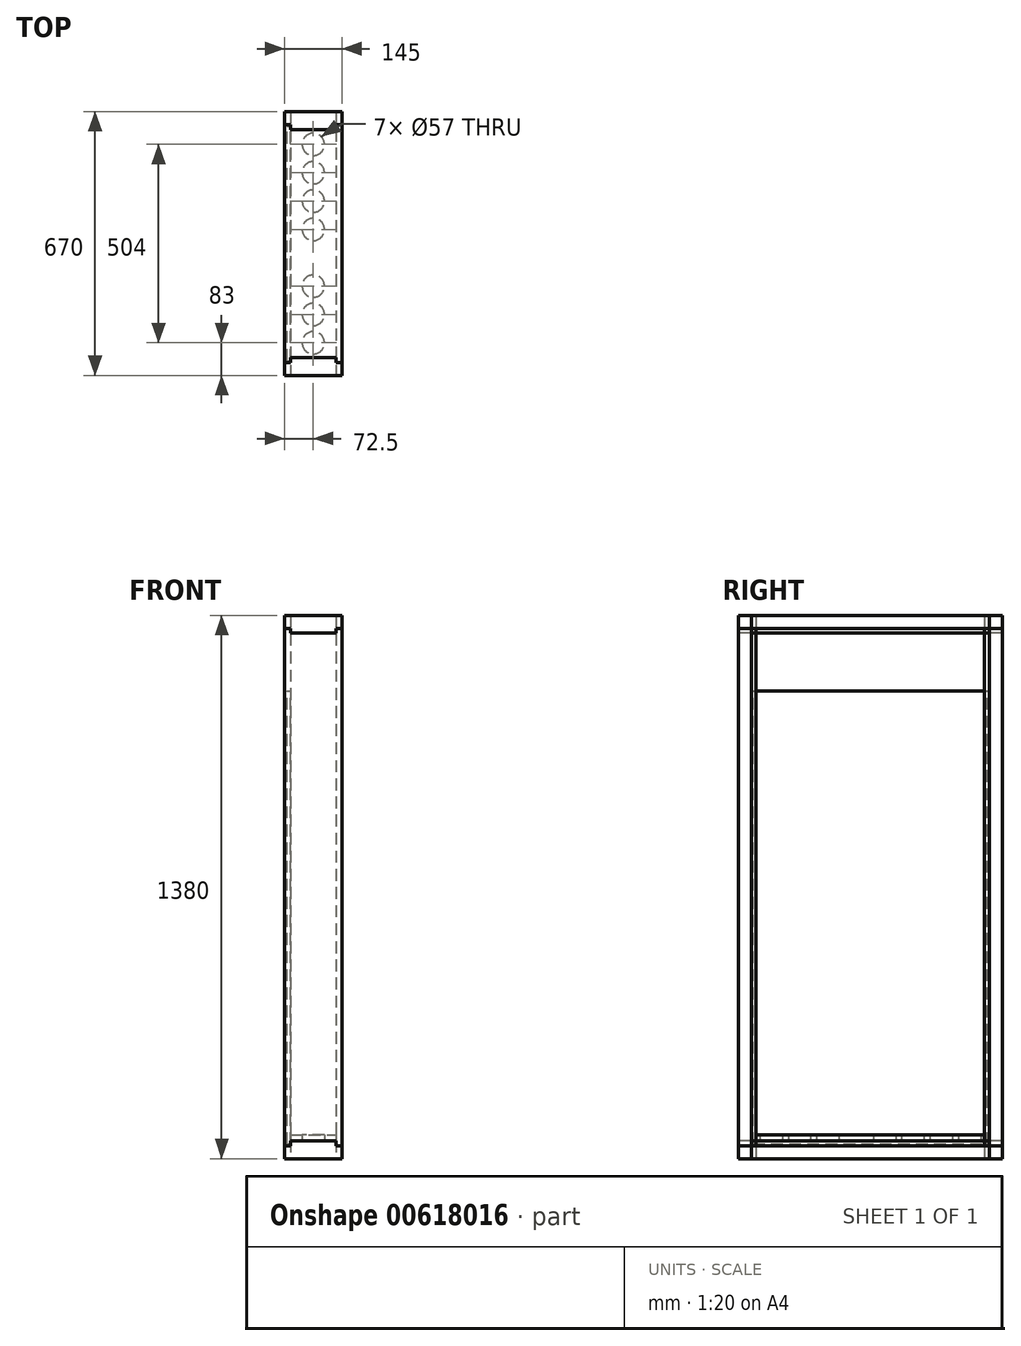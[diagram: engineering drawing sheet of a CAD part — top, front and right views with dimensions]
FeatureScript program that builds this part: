
annotation { "Feature Type Name" : "Feature", "Feature Type Description" : "" }
export const myFeature = defineFeature(function(context is Context, id is Id, definition is map)
    precondition{}
    {
        {
            var Q0;
            Q0=qCreatedBy(makeId("Top.planeOp"),FACE);
            var sketch = newSketch(context, id + "F0", { "sketchPlane" : qUnion([Q0])});
            skLineSegment(sketch, "E0.bottom", {"start": v(0, 0) * mm, "end": v(145, 0) * mm});
            skLineSegment(sketch, "E0.top", {"start": v(15, 45) * mm, "end": v(130, 45) * mm});
            skLineSegment(sketch, "E0.left", {"start": v(0, 0) * mm, "end": v(0, 33) * mm});
            skLineSegment(sketch, "E0.right", {"start": v(145, 0) * mm, "end": v(145, 33) * mm});
            skLineSegment(sketch, "E1.0", {"start": v(15, 33) * mm, "end": v(15, 45) * mm});
            skLineSegment(sketch, "E2.0", {"start": v(0, 33) * mm, "end": v(15, 33) * mm});
            skLineSegment(sketch, "E3.MirrorCS", {"start": v(145, 33) * mm, "end": v(130, 33) * mm});
            skLineSegment(sketch, "E4.MirrorCS", {"start": v(130, 33) * mm, "end": v(130, 45) * mm});
            skPoint(sketch, "E5.start.orphan", {"position": v(72.5, 0) * mm});
            skPoint(sketch, "E6.MirrorCS.end.orphan", {"position": v(15, 21) * mm});
            skPoint(sketch, "E6.MirrorCS.start.orphan", {"position": v(15, 33) * mm});
            skLineSegment(sketch, "E7", {"start": v(0, 335) * mm, "end": v(194.29, 335) * mm});
            skPoint(sketch, "E7.endSnap0", {"position": v(0, 335) * mm});
            skLineSegment(sketch, "E8.MirrorCS", {"start": v(0, 670) * mm, "end": v(145, 670) * mm});
            skLineSegment(sketch, "E9.MirrorCS", {"start": v(145, 670) * mm, "end": v(145, 637) * mm});
            skLineSegment(sketch, "E10.MirrorCS", {"start": v(145, 637) * mm, "end": v(130, 637) * mm});
            skLineSegment(sketch, "E11.MirrorCS", {"start": v(130, 637) * mm, "end": v(130, 625) * mm});
            skLineSegment(sketch, "E12.MirrorCS", {"start": v(15, 625) * mm, "end": v(130, 625) * mm});
            skLineSegment(sketch, "E13.MirrorCS", {"start": v(15, 637) * mm, "end": v(15, 625) * mm});
            skLineSegment(sketch, "E14.MirrorCS", {"start": v(0, 637) * mm, "end": v(15, 637) * mm});
            skLineSegment(sketch, "E15", {"start": v(0, 670) * mm, "end": v(0, 637) * mm});
            skSolve(sketch);
        }
        {
            var Q0;
            Q0=makeQuery(id+"F0.imprint","IMPRINT",FACE,{"disambiguationData":[TD([[makeQuery(id+"F0.imprint","IMPRINT",EDGE,{"derivedFrom":sQuery(id+"F0.wireOp",EDGE,"E0.bottom")}),1.0]])]});
            var Q1;
            Q1 = qSketchRegion(id + "F0", true);
            extrude(context, id + "F1", {"entities" : qUnion([Q0, Q1]), "depth" : 1380 * mm, "offsetDistance" : 25 * mm});
        }
        {
            var Q0;
            Q0=makeQuery(id+"F1.opExtrude","SWEPT_FACE",FACE,{"disambiguationData":[OSD([sQuery(id+"F0.wireOp",EDGE,"E0.bottom")])]});
            var sketch = newSketch(context, id + "F2", { "sketchPlane" : qUnion([Q0])});
            skLineSegment(sketch, "E16.bottom", {"start": v(0, 0) * mm, "end": v(145, 0) * mm});
            skLineSegment(sketch, "E16.top", {"start": v(15, 45) * mm, "end": v(130, 45) * mm});
            skLineSegment(sketch, "E16.left", {"start": v(0, 0) * mm, "end": v(0, 33) * mm});
            skLineSegment(sketch, "E16.right", {"start": v(145, 0) * mm, "end": v(145, 33) * mm});
            skLineSegment(sketch, "E17.0", {"start": v(15, 33) * mm, "end": v(15, 45) * mm});
            skLineSegment(sketch, "E18.0", {"start": v(0, 33) * mm, "end": v(15, 33) * mm});
            skLineSegment(sketch, "E19.MirrorCS", {"start": v(145, 33) * mm, "end": v(130, 33) * mm});
            skLineSegment(sketch, "E20.MirrorCS", {"start": v(130, 33) * mm, "end": v(130, 45) * mm});
            skPoint(sketch, "E21.orphan", {"position": v(145, 45) * mm});
            skPoint(sketch, "E22.orphan", {"position": v(0, 45) * mm});
            skLineSegment(sketch, "E23", {"start": v(0, 0) * mm, "end": v(0, 1380) * mm});
            skLineSegment(sketch, "E24", {"start": v(0, 690) * mm, "end": v(338.5, 690) * mm});
            skPoint(sketch, "E24.endSnap0", {"position": v(0, 690) * mm});
            skLineSegment(sketch, "E25.MirrorCS", {"start": v(15, 1347) * mm, "end": v(15, 1335) * mm});
            skLineSegment(sketch, "E26.MirrorCS", {"start": v(0, 1347) * mm, "end": v(15, 1347) * mm});
            skLineSegment(sketch, "E27.MirrorCS", {"start": v(0, 1380) * mm, "end": v(145, 1380) * mm});
            skLineSegment(sketch, "E28.MirrorCS", {"start": v(0, 1380) * mm, "end": v(0, 1347) * mm});
            skLineSegment(sketch, "E29.MirrorCS", {"start": v(130, 1347) * mm, "end": v(130, 1335) * mm});
            skLineSegment(sketch, "E30.MirrorCS", {"start": v(145, 1347) * mm, "end": v(130, 1347) * mm});
            skLineSegment(sketch, "E31.MirrorCS", {"start": v(145, 1380) * mm, "end": v(145, 1347) * mm});
            skLineSegment(sketch, "E32", {"start": v(15, 1335) * mm, "end": v(130, 1335) * mm});
            skSolve(sketch);
        }
        {
            var Q0;
            Q0=makeQuery(id+"F2.imprint","IMPRINT",FACE,{"disambiguationData":[TD([[makeQuery(id+"F2.imprint","IMPRINT",EDGE,{"derivedFrom":sQuery(id+"F2.wireOp",EDGE,"E25.MirrorCS")}),1.0]])]});
            var Q1;
            {var subQ0=sQuery(id+"F2.wireOp",EDGE,"E16.bottom");Q1=makeQuery(id+"F2.imprint","IMPRINT",FACE,{"disambiguationData":[TD([[makeQuery(id+"F2.imprint","IMPRINT",EDGE,{"derivedFrom":subQ0}),1.0]])]});}
            extrude(context, id + "F3", {"entities" : qUnion([Q0, Q1]), "oppositeDirection" : true, "depth" : 670 * mm, "offsetDistance" : 25 * mm});
        }
        {
            var Q0;
            Q0=makeQuery(id+"F3.opExtrude","SWEPT_FACE",FACE,{"disambiguationData":[OSD([sQuery(id+"F2.wireOp",EDGE,"E16.top")])]});
            var sketch = newSketch(context, id + "F4", { "sketchPlane" : qUnion([Q0])});
            skLineSegment(sketch, "E33", {"start": v(130, 625) * mm, "end": v(130, 45) * mm});
            skLineSegment(sketch, "E34", {"start": v(15, 45) * mm, "end": v(15, 625) * mm});
            skLineSegment(sketch, "E35.0", {"start": v(15, 625) * mm, "end": v(130, 625) * mm});
            skLineSegment(sketch, "E36.0", {"start": v(130, 45) * mm, "end": v(15, 45) * mm});
            skLineSegment(sketch, "E37", {"start": v(72.5, 45) * mm, "end": v(72.5, 625) * mm});
            skPoint(sketch, "E38.endSnap0", {"position": v(72.5, 335) * mm});
            skLineSegment(sketch, "E39.0", {"start": v(72.5, 299) * mm, "end": v(93.74, 299) * mm});
            skLineSegment(sketch, "E40.0.1.0", {"start": v(72.5, 227) * mm, "end": v(93.74, 227) * mm});
            skLineSegment(sketch, "E40.0.2.0", {"start": v(72.5, 155) * mm, "end": v(93.74, 155) * mm});
            skLineSegment(sketch, "E40.0.3.0", {"start": v(72.5, 83) * mm, "end": v(93.74, 83) * mm});
            skLineSegment(sketch, "E40.direction1", {"start": v(72.5, 299) * mm, "end": v(97.5, 299) * mm, "construction": true});
            skLineSegment(sketch, "E40.direction2", {"start": v(72.5, 299) * mm, "end": v(72.5, 227) * mm, "construction": true});
            skLineSegment(sketch, "E41.0.1.0", {"start": v(72.5, 371) * mm, "end": v(97.5, 371) * mm, "construction": true});
            skLineSegment(sketch, "E41.0.2.0", {"start": v(72.5, 443) * mm, "end": v(97.5, 443) * mm, "construction": true});
            skLineSegment(sketch, "E41.0.3.0", {"start": v(72.5, 515) * mm, "end": v(97.5, 515) * mm, "construction": true});
            skLineSegment(sketch, "E41.0.4.0", {"start": v(72.5, 587) * mm, "end": v(97.5, 587) * mm, "construction": true});
            skLineSegment(sketch, "E41.direction2", {"start": v(72.5, 299) * mm, "end": v(72.5, 371) * mm, "construction": true});
            skSolve(sketch);
        }
        {
            var Q0;
            Q0=makeQuery(id+"F4.imprint","IMPRINT",FACE,{"disambiguationData":[TD([[makeQuery(id+"F4.imprint","IMPRINT",EDGE,{"derivedFrom":sQuery(id+"F4.wireOp",EDGE,"E33")}),-1.0]])]});
            var Q1;
            {var subQ1=sQuery(id+"F4.wireOp",EDGE,"E34");Q1=makeQuery(id+"F4.imprint","IMPRINT",FACE,{"disambiguationData":[TD([[makeQuery(id+"F4.imprint","IMPRINT",EDGE,{"derivedFrom":subQ1}),1.0]])]});}
            extrude(context, id + "F5", {"entities" : qUnion([Q0, Q1]), "depth" : 16 * mm, "offsetDistance" : 25 * mm});
        }
        {
            var Q0;
            Q0=sQuery(id+"F4.wireOp",VERTEX,"E40.0.3.0.start");
            var Q1;
            Q1=sQuery(id+"F4.wireOp",VERTEX,"E40.0.2.0.start");
            var Q2;
            Q2=sQuery(id+"F4.wireOp",VERTEX,"E40.direction2.end");
            var Q3;
            Q3=sQuery(id+"F4.wireOp",VERTEX,"E40.direction1.start");
            var Q4;
            Q4=sQuery(id+"F4.wireOp",VERTEX,"E41.direction2.end");
            var Q5;
            Q5=sQuery(id+"F4.wireOp",VERTEX,"E41.0.2.0.start");
            var Q6;
            Q6=sQuery(id+"F4.wireOp",VERTEX,"E41.0.3.0.start");
            var Q7;
            Q7=sQuery(id+"F4.wireOp",VERTEX,"E41.0.4.0.start");
            var Q8;
            Q8=makeQuery(id+"F5.opExtrude","SWEPT_BODY",BODY,{"disambiguationData":[OSD([sQuery(id+"F4.wireOp",EDGE,"E33"),sQuery(id+"F4.wireOp",EDGE,"E34"),sQuery(id+"F4.wireOp",EDGE,"E35.0"),sQuery(id+"F4.wireOp",EDGE,"E36.0")])]});
            hole(context, id + "F6", {"style" : HoleStyle.SIMPLE, "endStyle" : HoleEndStyle.THROUGH, "oppositeDirection" : true, "holeDiameter" : 57 * mm, "majorDiameter" : 5 * mm, "isTappedThrough" : true, "tappedDepth" : 12 * mm, "tapClearance" : 3, "startFromSketch" : true, "locations" : qUnion([Q0, Q1, Q2, Q3, Q4, Q5, Q6, Q7]), "scope" : qUnion([Q8])});
        }
        {
            var Q0;
            Q0=makeQuery(id+"F3.opExtrude","SWEPT_FACE",FACE,{"disambiguationData":[OSD([sQuery(id+"F2.wireOp",EDGE,"E17.0")])]});
            var sketch = newSketch(context, id + "F7", { "sketchPlane" : qUnion([Q0])});
            skLineSegment(sketch, "E42.0", {"start": v(-37, 0) * mm, "end": v(-37, 1385.9) * mm});
            skLineSegment(sketch, "E43.0", {"start": v(0, 37) * mm, "end": v(-670, 37) * mm});
            skLineSegment(sketch, "E44.0", {"start": v(-633, 0) * mm, "end": v(-633, 1385.9) * mm});
            skLineSegment(sketch, "E45.0", {"start": v(0, 1343.9) * mm, "end": v(-670, 1343.9) * mm});
            skLineSegment(sketch, "E46.0", {"start": v(0, 1188) * mm, "end": v(-670, 1188) * mm});
            skSolve(sketch);
        }
        {
            var Q0;
            {var subQ0=sQuery(id+"F7.wireOp",EDGE,"E43.0");var subQ1=sQuery(id+"F7.wireOp",EDGE,"E42.0");var subQ2=makeQuery(id+"F7.imprint","INTERSECT",VERTEX,{"derivedFrom":[subQ1,subQ0]});Q0=makeQuery(id+"F7.imprint","IMPRINT",FACE,{"disambiguationData":[TD([[makeQuery(id+"F7.imprint","IMPRINT",EDGE,{"disambiguationData":[TD([[subQ2,-1.0]])],"derivedFrom":subQ0}),-1.0]])]});}
            var Q1;
            {var subQ0=sQuery(id+"F7.wireOp",EDGE,"E46.0");var subQ1=sQuery(id+"F7.wireOp",EDGE,"E42.0");var subQ2=makeQuery(id+"F7.imprint","INTERSECT",VERTEX,{"derivedFrom":[subQ1,subQ0]});Q1=makeQuery(id+"F7.imprint","IMPRINT",FACE,{"disambiguationData":[TD([[makeQuery(id+"F7.imprint","IMPRINT",EDGE,{"disambiguationData":[TD([[subQ2,-1.0]])],"derivedFrom":subQ0}),1.0]])]});}
            extrude(context, id + "F8", {"entities" : qUnion([Q0, Q1]), "depth" : 9 * mm, "offsetDistance" : 25 * mm});
        }
    });
